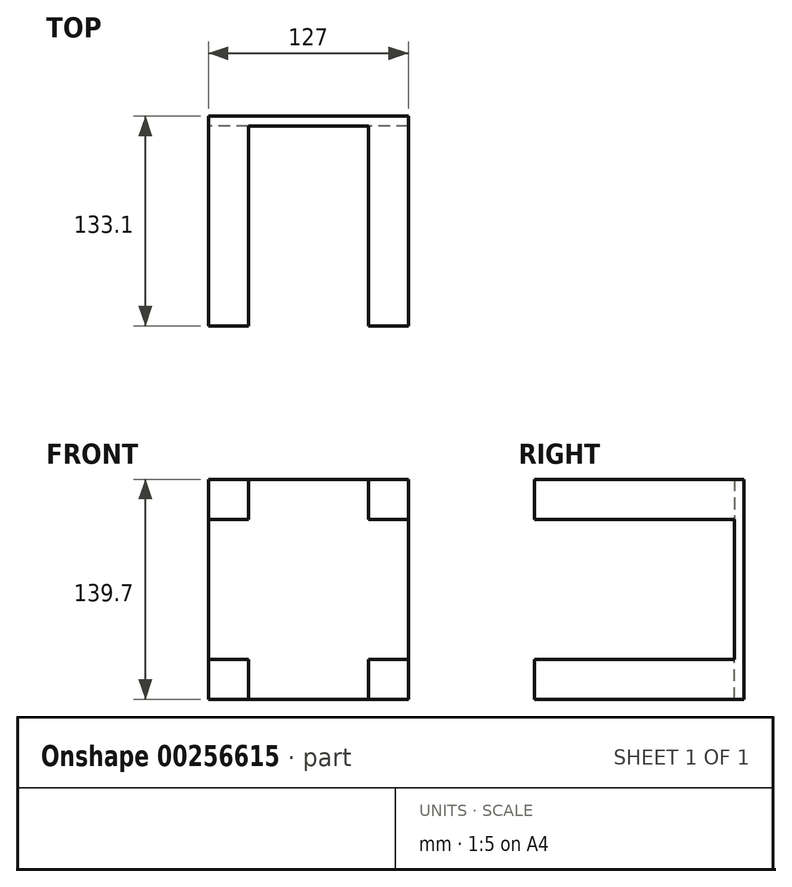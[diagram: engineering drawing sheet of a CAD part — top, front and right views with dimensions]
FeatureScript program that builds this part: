
annotation { "Feature Type Name" : "Feature", "Feature Type Description" : "" }
export const myFeature = defineFeature(function(context is Context, id is Id, definition is map)
    precondition{}
    {
        {
            var Q0;
            Q0=qCreatedBy(makeId("Front.planeOp"),FACE);
            var sketch = newSketch(context, id + "F0", { "sketchPlane" : qUnion([Q0])});
            skLineSegment(sketch, "E0.bottom", {"start": v(63.5, 69.85) * mm, "end": v(-63.5, 69.85) * mm});
            skLineSegment(sketch, "E0.top", {"start": v(63.5, -69.85) * mm, "end": v(-63.5, -69.85) * mm});
            skLineSegment(sketch, "E0.left", {"start": v(63.5, 69.85) * mm, "end": v(63.5, -69.85) * mm});
            skLineSegment(sketch, "E0.right", {"start": v(-63.5, 69.85) * mm, "end": v(-63.5, -69.85) * mm});
            skPoint(sketch, "E0.middle", {"position": v(0, 0) * mm});
            skSolve(sketch);
        }
        {
            var Q0;
            Q0=makeQuery(id+"F0.imprint","IMPRINT",FACE,{"disambiguationData":[TD([[makeQuery(id+"F0.imprint","IMPRINT",EDGE,{"derivedFrom":sQuery(id+"F0.wireOp",EDGE,"E0.bottom")}),1.0]])]});
            extrude(context, id + "F1", {"entities" : qUnion([Q0]), "depth" : 6.1 * mm});
        }
        {
            var Q0;
            Q0=makeQuery(id+"F1.opExtrude","CAP_FACE",FACE,{"disambiguationData":[OSD([sQuery(id+"F0.wireOp",EDGE,"E0.bottom"),sQuery(id+"F0.wireOp",EDGE,"E0.top"),sQuery(id+"F0.wireOp",EDGE,"E0.left"),sQuery(id+"F0.wireOp",EDGE,"E0.right")])],"isStart":false});
            var sketch = newSketch(context, id + "F2", { "sketchPlane" : qUnion([Q0])});
            skLineSegment(sketch, "E1.bottom", {"start": v(-38.1, 69.85) * mm, "end": v(-63.5, 69.85) * mm});
            skLineSegment(sketch, "E1.top", {"start": v(-38.1, 44.45) * mm, "end": v(-63.5, 44.45) * mm});
            skLineSegment(sketch, "E1.left", {"start": v(-38.1, 69.85) * mm, "end": v(-38.1, 44.45) * mm});
            skLineSegment(sketch, "E1.right", {"start": v(-63.5, 69.85) * mm, "end": v(-63.5, 44.45) * mm});
            skPoint(sketch, "E1.middle", {"position": v(-50.8, 57.15) * mm});
            skLineSegment(sketch, "E2.bottom", {"start": v(63.5, 69.85) * mm, "end": v(38.1, 69.85) * mm});
            skLineSegment(sketch, "E2.top", {"start": v(63.5, 44.45) * mm, "end": v(38.1, 44.45) * mm});
            skLineSegment(sketch, "E2.left", {"start": v(63.5, 69.85) * mm, "end": v(63.5, 44.45) * mm});
            skLineSegment(sketch, "E2.right", {"start": v(38.1, 69.85) * mm, "end": v(38.1, 44.45) * mm});
            skLineSegment(sketch, "E3.bottom", {"start": v(-63.5, -69.85) * mm, "end": v(-38.1, -69.85) * mm});
            skLineSegment(sketch, "E3.top", {"start": v(-63.5, -44.45) * mm, "end": v(-38.1, -44.45) * mm});
            skLineSegment(sketch, "E3.left", {"start": v(-63.5, -69.85) * mm, "end": v(-63.5, -44.45) * mm});
            skLineSegment(sketch, "E3.right", {"start": v(-38.1, -69.85) * mm, "end": v(-38.1, -44.45) * mm});
            skLineSegment(sketch, "E4.bottom", {"start": v(63.5, -69.85) * mm, "end": v(38.1, -69.85) * mm});
            skLineSegment(sketch, "E4.top", {"start": v(63.5, -44.45) * mm, "end": v(38.1, -44.45) * mm});
            skLineSegment(sketch, "E4.left", {"start": v(63.5, -69.85) * mm, "end": v(63.5, -44.45) * mm});
            skLineSegment(sketch, "E4.right", {"start": v(38.1, -69.85) * mm, "end": v(38.1, -44.45) * mm});
            skSolve(sketch);
        }
        {
            var Q0;
            Q0=makeQuery(id+"F2.imprint","IMPRINT",FACE,{"disambiguationData":[TD([[makeQuery(id+"F2.imprint","IMPRINT",EDGE,{"derivedFrom":sQuery(id+"F2.wireOp",EDGE,"E1.bottom")}),1.0]])]});
            extrude(context, id + "F3", {"entities" : qUnion([Q0]), "operationType" : NewBodyOperationType.ADD, "depth" : 127 * mm});
        }
        {
            var Q0;
            Q0=makeQuery(id+"F2.imprint","IMPRINT",FACE,{"disambiguationData":[TD([[makeQuery(id+"F2.imprint","IMPRINT",EDGE,{"derivedFrom":sQuery(id+"F2.wireOp",EDGE,"E3.bottom")}),-1.0]])]});
            extrude(context, id + "F4", {"entities" : qUnion([Q0]), "operationType" : NewBodyOperationType.ADD, "depth" : 127 * mm});
        }
        {
            var Q0;
            Q0=makeQuery(id+"F2.imprint","IMPRINT",FACE,{"disambiguationData":[TD([[makeQuery(id+"F2.imprint","IMPRINT",EDGE,{"derivedFrom":sQuery(id+"F2.wireOp",EDGE,"E2.bottom")}),1.0]])]});
            extrude(context, id + "F5", {"entities" : qUnion([Q0]), "operationType" : NewBodyOperationType.ADD, "depth" : 127 * mm});
        }
        {
            var Q0;
            Q0=makeQuery(id+"F2.imprint","IMPRINT",FACE,{"disambiguationData":[TD([[makeQuery(id+"F2.imprint","IMPRINT",EDGE,{"derivedFrom":sQuery(id+"F2.wireOp",EDGE,"E4.bottom")}),-1.0]])]});
            extrude(context, id + "F6", {"entities" : qUnion([Q0]), "operationType" : NewBodyOperationType.ADD, "depth" : 127 * mm});
        }
    });
